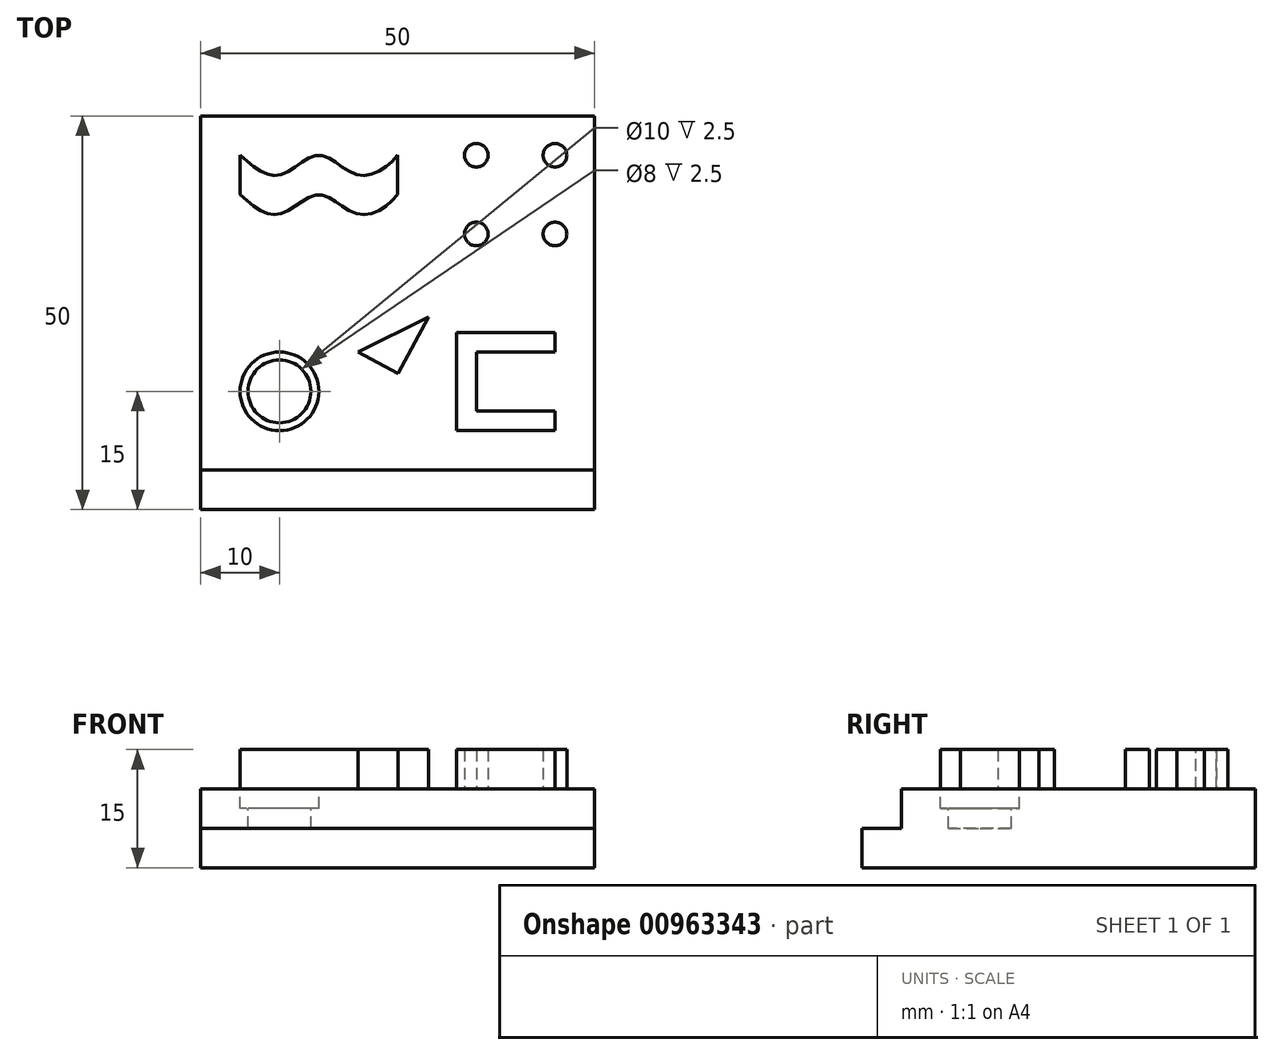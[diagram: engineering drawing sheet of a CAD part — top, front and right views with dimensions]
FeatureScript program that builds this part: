
annotation { "Feature Type Name" : "Feature", "Feature Type Description" : "" }
export const myFeature = defineFeature(function(context is Context, id is Id, definition is map)
    precondition{}
    {
        {
            var Q0;
            Q0=qCreatedBy(makeId("Top.planeOp"),FACE);
            var sketch = newSketch(context, id + "F0", { "sketchPlane" : qUnion([Q0])});
            skLineSegment(sketch, "E0.bottom", {"start": v(-50, 0) * mm, "end": v(0, 0) * mm});
            skLineSegment(sketch, "E0.top", {"start": v(-50, 50) * mm, "end": v(0, 50) * mm});
            skLineSegment(sketch, "E0.left", {"start": v(-50, 0) * mm, "end": v(-50, 50) * mm});
            skLineSegment(sketch, "E0.right", {"start": v(0, 0) * mm, "end": v(0, 50) * mm});
            skSolve(sketch);
        }
        {
            var Q0;
            Q0=makeQuery(id+"F0.imprint","IMPRINT",FACE,{"disambiguationData":[TD([[makeQuery(id+"F0.imprint","IMPRINT",EDGE,{"derivedFrom":sQuery(id+"F0.wireOp",EDGE,"E0.bottom")}),1.0]])]});
            extrude(context, id + "F1", {"entities" : qUnion([Q0]), "depth" : 5 * mm, "offsetDistance" : 25 * mm});
        }
        {
            var Q0;
            Q0=makeQuery(id+"F1.opExtrude","CAP_FACE",FACE,{"disambiguationData":[OSD([sQuery(id+"F0.wireOp",EDGE,"E0.bottom"),sQuery(id+"F0.wireOp",EDGE,"E0.top"),sQuery(id+"F0.wireOp",EDGE,"E0.left"),sQuery(id+"F0.wireOp",EDGE,"E0.right")])],"isStart":false});
            var sketch = newSketch(context, id + "F2", { "sketchPlane" : qUnion([Q0])});
            skLineSegment(sketch, "E1.bottom", {"start": v(-50, 5) * mm, "end": v(0, 5) * mm});
            skLineSegment(sketch, "E1.top", {"start": v(-50, 50) * mm, "end": v(0, 50) * mm});
            skLineSegment(sketch, "E1.left", {"start": v(-50, 5) * mm, "end": v(-50, 50) * mm});
            skLineSegment(sketch, "E1.right", {"start": v(0, 5) * mm, "end": v(0, 50) * mm});
            skSolve(sketch);
        }
        {
            var Q0;
            Q0=makeQuery(id+"F2.imprint","IMPRINT",FACE,{"disambiguationData":[TD([[makeQuery(id+"F2.imprint","IMPRINT",EDGE,{"derivedFrom":sQuery(id+"F2.wireOp",EDGE,"E1.bottom")}),1.0]])]});
            extrude(context, id + "F3", {"entities" : qUnion([Q0]), "operationType" : NewBodyOperationType.ADD, "depth" : 5 * mm, "offsetDistance" : 25 * mm});
        }
        {
            var Q0;
            Q0=makeQuery(id+"F3.opExtrude","CAP_FACE",FACE,{"disambiguationData":[OSD([sQuery(id+"F2.wireOp",EDGE,"E1.bottom"),sQuery(id+"F2.wireOp",EDGE,"E1.top"),sQuery(id+"F2.wireOp",EDGE,"E1.left"),sQuery(id+"F2.wireOp",EDGE,"E1.right")])],"isStart":false});
            var sketch = newSketch(context, id + "F4", { "sketchPlane" : qUnion([Q0])});
            skCircle(sketch, "E2", {"center": v(-40, 15) * mm, "radius": 5 * mm});
            skCircle(sketch, "E3", {"center": v(-40, 15) * mm, "radius": 4 * mm});
            skSolve(sketch);
        }
        {
            var Q0;
            Q0=makeQuery(id+"F4.imprint","IMPRINT",FACE,{"disambiguationData":[TD([[makeQuery(id+"F4.imprint","IMPRINT",EDGE,{"derivedFrom":sQuery(id+"F4.wireOp",EDGE,"E2")}),1.0]])]});
            var Q1;
            Q1=sQuery(id+"F4.wireOp",EDGE,"E2");
            extrude(context, id + "F5", {"entities" : qUnion([Q0]), "operationType" : NewBodyOperationType.REMOVE, "surfaceEntities" : qUnion([Q1]), "oppositeDirection" : true, "depth" : 2.5 * mm, "offsetDistance" : 25 * mm});
        }
        {
            var Q0;
            Q0=makeQuery(id+"F5.boolean.opBoolean","SPLIT",FACE,{"disambiguationData":[TD([makeQuery(id+"F5.opExtrude","SWEPT_FACE",FACE,{"disambiguationData":[OSD([sQuery(id+"F4.wireOp",EDGE,"E3")])]})])],"derivedFrom":makeQuery(id+"F3.opExtrude","CAP_FACE",FACE,{"disambiguationData":[OSD([sQuery(id+"F2.wireOp",EDGE,"E1.bottom"),sQuery(id+"F2.wireOp",EDGE,"E1.top"),sQuery(id+"F2.wireOp",EDGE,"E1.left"),sQuery(id+"F2.wireOp",EDGE,"E1.right")])],"isStart":false})});
            extrude(context, id + "F6", {"entities" : qUnion([Q0]), "operationType" : NewBodyOperationType.REMOVE, "oppositeDirection" : true, "depth" : 5 * mm, "offsetDistance" : 25 * mm});
        }
        {
            var Q0;
            {var subQ0=sQuery(id+"F2.wireOp",EDGE,"E1.left");var subQ1=sQuery(id+"F2.wireOp",EDGE,"E1.top");var subQ2=sQuery(id+"F2.wireOp",EDGE,"E1.bottom");var subQ3=sQuery(id+"F2.wireOp",EDGE,"E1.right");Q0=makeQuery(id+"F5.boolean.opBoolean","SPLIT",FACE,{"disambiguationData":[TD([makeQuery(id+"F1.opExtrude","SWEPT_FACE",FACE,{"disambiguationData":[OSD([sQuery(id+"F0.wireOp",EDGE,"E0.top")])]})])],"derivedFrom":makeQuery(id+"F3.opExtrude","CAP_FACE",FACE,{"disambiguationData":[OSD([subQ2,subQ1,subQ0,subQ3])],"isStart":false})});}
            var sketch = newSketch(context, id + "F7", { "sketchPlane" : qUnion([Q0])});
            skCircle(sketch, "E4", {"center": v(-5, 45) * mm, "radius": 1.5 * mm});
            skCircle(sketch, "E5", {"center": v(-15, 45) * mm, "radius": 1.5 * mm});
            skCircle(sketch, "E6", {"center": v(-5, 35) * mm, "radius": 1.5 * mm});
            skCircle(sketch, "E7", {"center": v(-15, 35) * mm, "radius": 1.5 * mm});
            skSolve(sketch);
        }
        {
            var Q0;
            Q0=makeQuery(id+"F7.imprint","IMPRINT",FACE,{"disambiguationData":[TD([[makeQuery(id+"F7.imprint","IMPRINT",EDGE,{"derivedFrom":sQuery(id+"F7.wireOp",EDGE,"E7")}),1.0]])]});
            var Q1;
            Q1=makeQuery(id+"F7.imprint","IMPRINT",FACE,{"disambiguationData":[TD([[makeQuery(id+"F7.imprint","IMPRINT",EDGE,{"derivedFrom":sQuery(id+"F7.wireOp",EDGE,"E6")}),1.0]])]});
            var Q2;
            Q2=makeQuery(id+"F7.imprint","IMPRINT",FACE,{"disambiguationData":[TD([[makeQuery(id+"F7.imprint","IMPRINT",EDGE,{"derivedFrom":sQuery(id+"F7.wireOp",EDGE,"E5")}),1.0]])]});
            var Q3;
            Q3=makeQuery(id+"F7.imprint","IMPRINT",FACE,{"disambiguationData":[TD([[makeQuery(id+"F7.imprint","IMPRINT",EDGE,{"derivedFrom":sQuery(id+"F7.wireOp",EDGE,"E4")}),1.0]])]});
            extrude(context, id + "F8", {"entities" : qUnion([Q0, Q1, Q2, Q3]), "operationType" : NewBodyOperationType.ADD, "depth" : 5 * mm, "offsetDistance" : 25 * mm});
        }
        {
            var Q0;
            {var subQ0=sQuery(id+"F2.wireOp",EDGE,"E1.left");var subQ1=sQuery(id+"F2.wireOp",EDGE,"E1.top");var subQ2=sQuery(id+"F2.wireOp",EDGE,"E1.bottom");var subQ3=sQuery(id+"F2.wireOp",EDGE,"E1.right");Q0=makeQuery(id+"F5.boolean.opBoolean","SPLIT",FACE,{"disambiguationData":[TD([makeQuery(id+"F1.opExtrude","SWEPT_FACE",FACE,{"disambiguationData":[OSD([sQuery(id+"F0.wireOp",EDGE,"E0.top")])]})])],"derivedFrom":makeQuery(id+"F3.opExtrude","CAP_FACE",FACE,{"disambiguationData":[OSD([subQ2,subQ1,subQ0,subQ3])],"isStart":false})});}
            var sketch = newSketch(context, id + "F9", { "sketchPlane" : qUnion([Q0])});
            skFitSpline(sketch, "E8", {"points": [v(-45, 45) * mm, v(-40, 42.5) * mm, v(-35, 45) * mm, v(-30, 42.5) * mm, v(-25, 45) * mm], "startDerivative": vector(19.53, -18.05) * mm, "endDerivative": vector(13.96, 18.38) * mm});
            skFitSpline(sketch, "E9", {"points": [v(-45, 40) * mm, v(-40, 37.5) * mm, v(-35, 40) * mm, v(-30, 37.5) * mm, v(-25, 40) * mm], "startDerivative": vector(19.53, -18.05) * mm, "endDerivative": vector(13.96, 18.38) * mm});
            skLineSegment(sketch, "E10", {"start": v(-45, 45) * mm, "end": v(-45, 40) * mm});
            skLineSegment(sketch, "E11", {"start": v(-25, 45) * mm, "end": v(-25, 40) * mm});
            skSolve(sketch);
        }
        {
            var Q0;
            Q0=makeQuery(id+"F9.imprint","IMPRINT",FACE,{"disambiguationData":[TD([[makeQuery(id+"F9.imprint","IMPRINT",EDGE,{"derivedFrom":sQuery(id+"F9.wireOp",EDGE,"E8")}),-1.0]])]});
            extrude(context, id + "F10", {"entities" : qUnion([Q0]), "operationType" : NewBodyOperationType.ADD, "depth" : 5 * mm, "offsetDistance" : 25 * mm});
        }
        {
            var Q0;
            {var subQ0=sQuery(id+"F2.wireOp",EDGE,"E1.left");var subQ1=sQuery(id+"F2.wireOp",EDGE,"E1.top");var subQ2=sQuery(id+"F2.wireOp",EDGE,"E1.bottom");var subQ3=sQuery(id+"F2.wireOp",EDGE,"E1.right");Q0=makeQuery(id+"F5.boolean.opBoolean","SPLIT",FACE,{"disambiguationData":[TD([makeQuery(id+"F1.opExtrude","SWEPT_FACE",FACE,{"disambiguationData":[OSD([sQuery(id+"F0.wireOp",EDGE,"E0.top")])]})])],"derivedFrom":makeQuery(id+"F3.opExtrude","CAP_FACE",FACE,{"disambiguationData":[OSD([subQ2,subQ1,subQ0,subQ3])],"isStart":false})});}
            var sketch = newSketch(context, id + "F11", { "sketchPlane" : qUnion([Q0])});
            skLineSegment(sketch, "E12", {"start": v(-30, 20) * mm, "end": v(-21.06, 24.47) * mm});
            skLineSegment(sketch, "E13", {"start": v(-21.06, 24.47) * mm, "end": v(-24.96, 17.27) * mm});
            skLineSegment(sketch, "E14", {"start": v(-24.96, 17.27) * mm, "end": v(-30, 20) * mm});
            skSolve(sketch);
        }
        {
            var Q0;
            Q0=makeQuery(id+"F11.imprint","IMPRINT",FACE,{"disambiguationData":[TD([[makeQuery(id+"F11.imprint","IMPRINT",EDGE,{"derivedFrom":sQuery(id+"F11.wireOp",EDGE,"E12")}),-1.0]])]});
            extrude(context, id + "F12", {"entities" : qUnion([Q0]), "operationType" : NewBodyOperationType.ADD, "depth" : 5 * mm, "offsetDistance" : 25 * mm});
        }
        {
            var Q0;
            {var subQ0=sQuery(id+"F2.wireOp",EDGE,"E1.left");var subQ1=sQuery(id+"F2.wireOp",EDGE,"E1.top");var subQ2=sQuery(id+"F2.wireOp",EDGE,"E1.bottom");var subQ3=sQuery(id+"F2.wireOp",EDGE,"E1.right");Q0=makeQuery(id+"F5.boolean.opBoolean","SPLIT",FACE,{"disambiguationData":[TD([makeQuery(id+"F1.opExtrude","SWEPT_FACE",FACE,{"disambiguationData":[OSD([sQuery(id+"F0.wireOp",EDGE,"E0.top")])]})])],"derivedFrom":makeQuery(id+"F3.opExtrude","CAP_FACE",FACE,{"disambiguationData":[OSD([subQ2,subQ1,subQ0,subQ3])],"isStart":false})});}
            var sketch = newSketch(context, id + "F13", { "sketchPlane" : qUnion([Q0])});
            skLineSegment(sketch, "E15.bottom", {"start": v(-5, 12.5) * mm, "end": v(-15, 12.5) * mm});
            skLineSegment(sketch, "E15.top", {"start": v(-5, 10) * mm, "end": v(-15, 10) * mm});
            skLineSegment(sketch, "E15.left", {"start": v(-5, 12.5) * mm, "end": v(-5, 10) * mm});
            skLineSegment(sketch, "E15.right", {"start": v(-15, 12.5) * mm, "end": v(-15, 10) * mm});
            skLineSegment(sketch, "E16.bottom", {"start": v(-5, 22.5) * mm, "end": v(-15, 22.5) * mm});
            skLineSegment(sketch, "E16.top", {"start": v(-5, 20) * mm, "end": v(-15, 20) * mm});
            skLineSegment(sketch, "E16.left", {"start": v(-5, 22.5) * mm, "end": v(-5, 20) * mm});
            skLineSegment(sketch, "E16.right", {"start": v(-15, 22.5) * mm, "end": v(-15, 20) * mm});
            skLineSegment(sketch, "E17.bottom", {"start": v(-15, 10) * mm, "end": v(-17.5, 10) * mm});
            skLineSegment(sketch, "E17.top", {"start": v(-15, 22.5) * mm, "end": v(-17.5, 22.5) * mm});
            skLineSegment(sketch, "E17.left", {"start": v(-15, 10) * mm, "end": v(-15, 22.5) * mm});
            skLineSegment(sketch, "E17.right", {"start": v(-17.5, 10) * mm, "end": v(-17.5, 22.5) * mm});
            skSolve(sketch);
        }
        {
            var Q0;
            {var subQ0=sQuery(id+"F13.wireOp",EDGE,"E16.bottom");Q0=makeQuery(id+"F13.imprint","IMPRINT",FACE,{"disambiguationData":[TD([[makeQuery(id+"F13.imprint","IMPRINT",EDGE,{"derivedFrom":subQ0}),1.0]])]});}
            var Q1;
            {var subQ3=sQuery(id+"F13.wireOp",EDGE,"E17.bottom");Q1=makeQuery(id+"F13.imprint","IMPRINT",FACE,{"disambiguationData":[TD([[makeQuery(id+"F13.imprint","IMPRINT",EDGE,{"derivedFrom":subQ3}),-1.0]])]});}
            var Q2;
            {var subQ0=sQuery(id+"F13.wireOp",EDGE,"E15.bottom");Q2=makeQuery(id+"F13.imprint","IMPRINT",FACE,{"disambiguationData":[TD([[makeQuery(id+"F13.imprint","IMPRINT",EDGE,{"derivedFrom":subQ0}),1.0]])]});}
            extrude(context, id + "F14", {"entities" : qUnion([Q0, Q1, Q2]), "operationType" : NewBodyOperationType.ADD, "depth" : 5 * mm, "offsetDistance" : 25 * mm});
        }
    });
